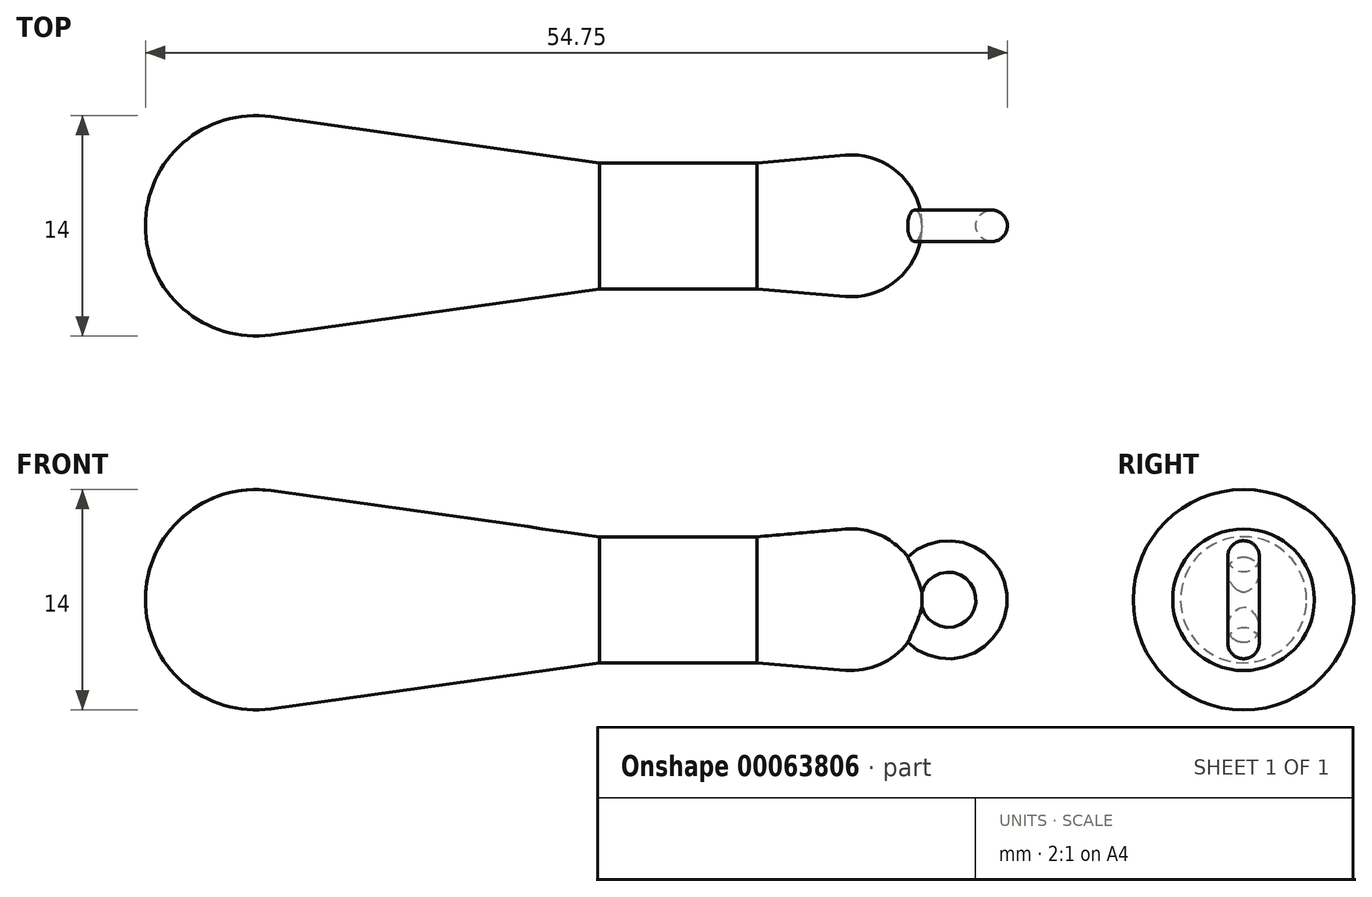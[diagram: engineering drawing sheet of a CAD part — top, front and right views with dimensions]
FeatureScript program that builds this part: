
annotation { "Feature Type Name" : "Feature", "Feature Type Description" : "" }
export const myFeature = defineFeature(function(context is Context, id is Id, definition is map)
    precondition{}
    {
        {
            var Q0;
            Q0=qCreatedBy(makeId("Front.planeOp"),FACE);
            var sketch = newSketch(context, id + "F0", { "sketchPlane" : qUnion([Q0])});
            skLineSegment(sketch, "E0", {"start": v(-7, 0) * mm, "end": v(42.34, 0) * mm});
            skArc(sketch, "E1", {"start": v(0.97, 6.93) * mm, "mid": v(-4.6, 5.28) * mm, "end": v(-7, 0) * mm});
            skArc(sketch, "E2", {"start": v(42.34, 0) * mm, "mid": v(40.88, 3.32) * mm, "end": v(37.45, 4.48) * mm});
            skLineSegment(sketch, "E3", {"start": v(0.97, 6.93) * mm, "end": v(21.84, 4) * mm});
            skLineSegment(sketch, "E4", {"start": v(31.84, 4) * mm, "end": v(37.45, 4.48) * mm});
            skLineSegment(sketch, "E5", {"start": v(21.84, 4) * mm, "end": v(31.84, 4) * mm});
            skSolve(sketch);
        }
        {
            var Q0;
            Q0=makeQuery(id+"F0.imprint","IMPRINT",FACE,{"disambiguationData":[TD([[makeQuery(id+"F0.imprint","IMPRINT",EDGE,{"derivedFrom":sQuery(id+"F0.wireOp",EDGE,"E0")}),1.0]])]});
            var Q1;
            Q1=sQuery(id+"F0.wireOp",EDGE,"E0");
            revolve(context, id + "F1", {"entities" : qUnion([Q0]), "axis" : qUnion([Q1]), "revolveType" : RevolveType.FULL});
        }
        {
            var Q0;
            Q0=qCreatedBy(makeId("Front.planeOp"),FACE);
            var sketch = newSketch(context, id + "F2", { "sketchPlane" : qUnion([Q0])});
            skCircle(sketch, "E6", {"center": v(44, 0) * mm, "radius": 1.75 * mm});
            skSolve(sketch);
        }
        {
            var Q0;
            Q0=qCreatedBy(makeId("Top.planeOp"),FACE);
            var sketch = newSketch(context, id + "F3", { "sketchPlane" : qUnion([Q0])});
            skCircle(sketch, "E7", {"center": v(46.75, 0) * mm, "radius": 1 * mm});
            skLineSegment(sketch, "E8", {"start": v(46.75, 0) * mm, "end": v(45.75, 0) * mm});
            skLineSegment(sketch, "E9.1", {"start": v(45.75, 0) * mm, "end": v(42.25, 0) * mm, "construction": true});
            skSolve(sketch);
        }
        {
            var Q0;
            Q0=makeQuery(id+"F3.imprint","IMPRINT",FACE,{"disambiguationData":[TD([[makeQuery(id+"F3.imprint","IMPRINT",EDGE,{"derivedFrom":sQuery(id+"F3.wireOp",EDGE,"E7")}),1.0]])]});
            var Q1;
            Q1=sQuery(id+"F2.wireOp",EDGE,"E6");
            sweep(context, id + "F4", {"operationType" : NewBodyOperationType.ADD, "profiles" : qUnion([Q0]), "path" : qUnion([Q1])});
        }
        {
            var Q0;
            Q0=qCreatedBy(makeId("Right.planeOp"),FACE);
            cPlane(context, id + "F5", {"entities" : qUnion([Q0]), "cplaneType" : CPlaneType.OFFSET, "offset" : 7 * mm, "oppositeDirection" : true, "width" : 150 * mm, "height" : 150 * mm});
        }
    });
